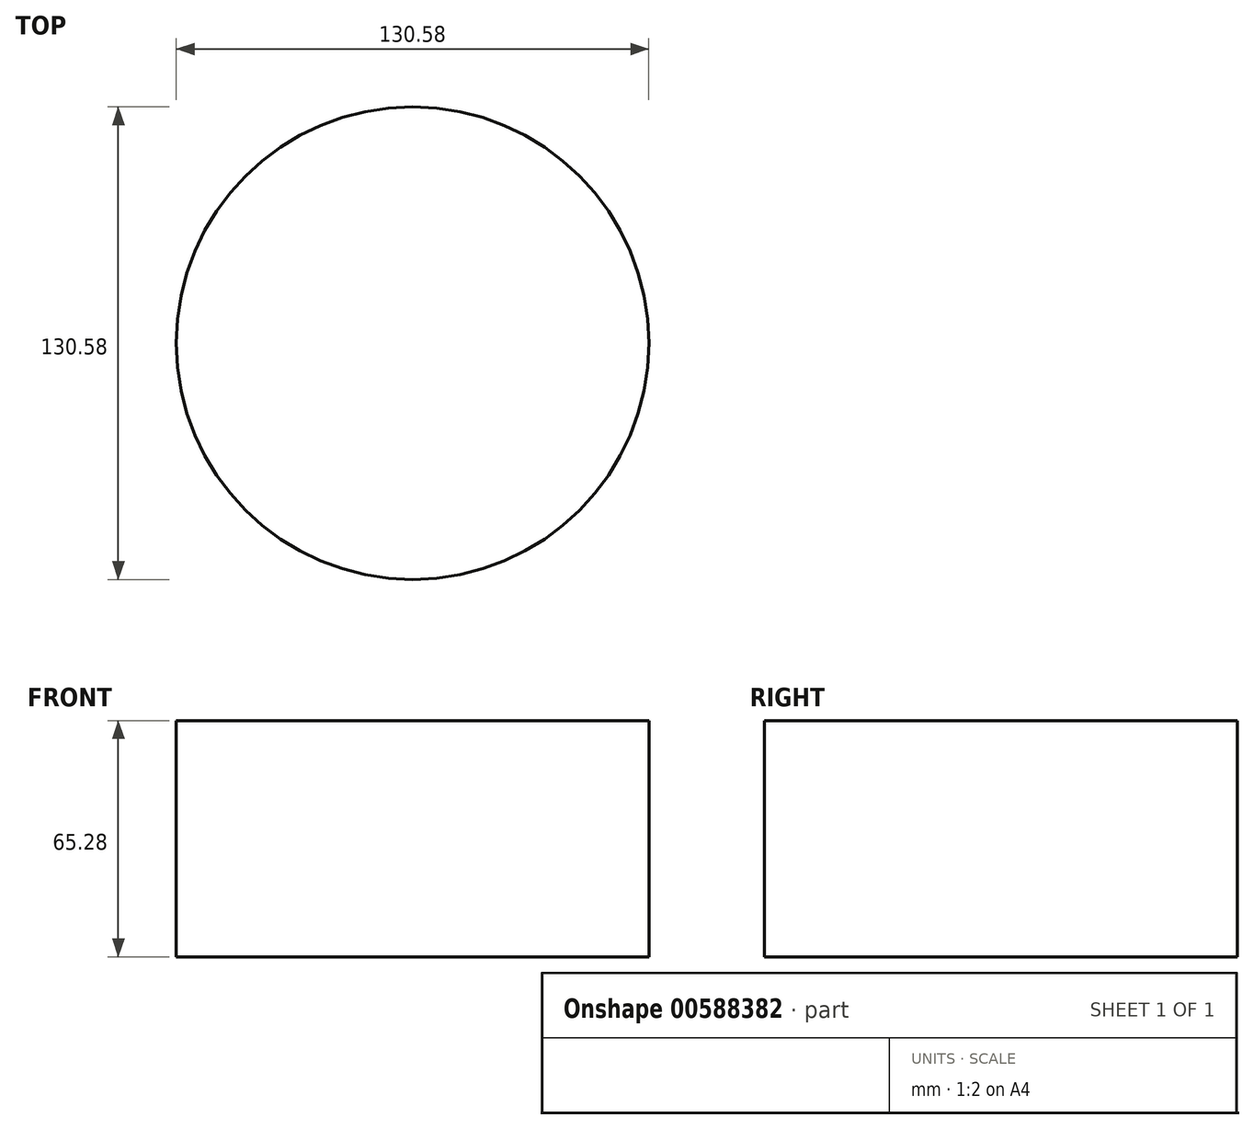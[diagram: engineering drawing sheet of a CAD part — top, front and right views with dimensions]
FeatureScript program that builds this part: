
annotation { "Feature Type Name" : "Feature", "Feature Type Description" : "" }
export const myFeature = defineFeature(function(context is Context, id is Id, definition is map)
    precondition{}
    {
        {
            var Q0;
            Q0=qCreatedBy(makeId("Top.planeOp"),FACE);
            var sketch = newSketch(context, id + "F0", { "sketchPlane" : qUnion([Q0])});
            skCircle(sketch, "E0", {"center": v(0, 0) * mm, "radius": 65.3 * mm});
            skSolve(sketch);
        }
        {
            var Q0;
            Q0=makeQuery(id+"F0.imprint","IMPRINT",FACE,{"disambiguationData":[TD([[makeQuery(id+"F0.imprint","IMPRINT",EDGE,{"derivedFrom":sQuery(id+"F0.wireOp",EDGE,"E0")}),1.0]])]});
            extrude(context, id + "F1", {"entities" : qUnion([Q0]), "depth" : 65.28 * mm, "offsetDistance" : 25.4 * mm});
        }
    });
